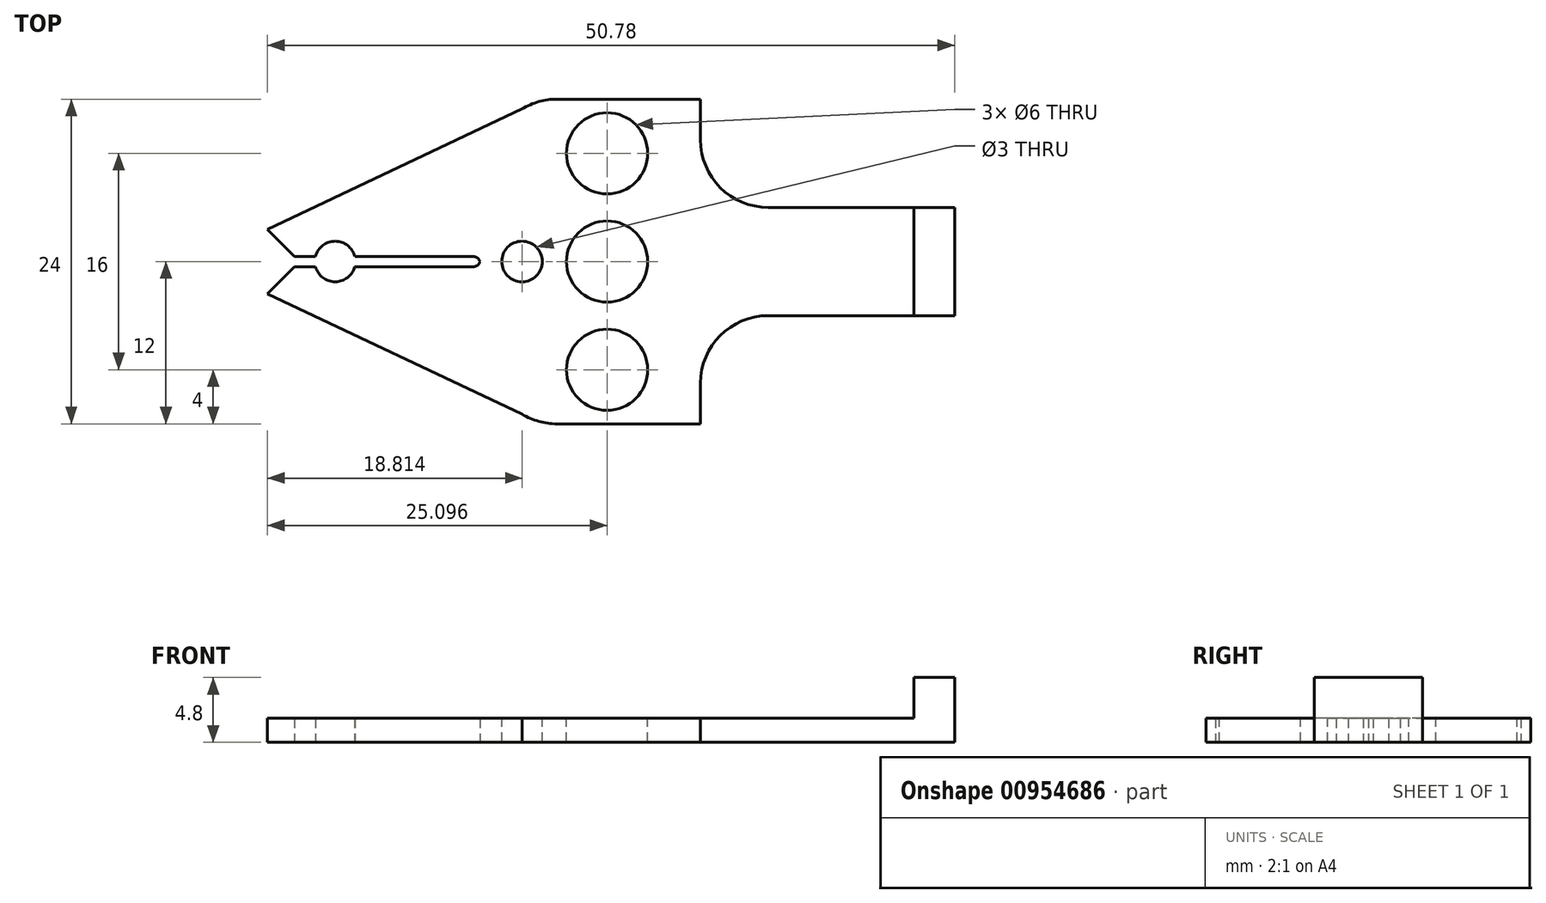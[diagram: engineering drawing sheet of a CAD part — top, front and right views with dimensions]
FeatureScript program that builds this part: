
annotation { "Feature Type Name" : "Feature", "Feature Type Description" : "" }
export const myFeature = defineFeature(function(context is Context, id is Id, definition is map)
    precondition{}
    {
        {
            var Q0;
            Q0=qCreatedBy(makeId("Top.planeOp"),FACE);
            var sketch = newSketch(context, id + "F0", { "sketchPlane" : qUnion([Q0])});
            skLineSegment(sketch, "E0.top", {"start": v(1.39, -12) * mm, "end": v(12, -12) * mm});
            skLineSegment(sketch, "E0.right", {"start": v(12, 12) * mm, "end": v(12, -12) * mm});
            skPoint(sketch, "E0.middle", {"position": v(0, 0) * mm});
            skArc(sketch, "E1", {"start": v(-16.45, -0.39) * mm, "mid": v(-15, -1.5) * mm, "end": v(-13.55, -0.39) * mm});
            skLineSegment(sketch, "E2", {"start": v(-18, 0.37) * mm, "end": v(-16.45, 0.37) * mm});
            skLineSegment(sketch, "E3", {"start": v(-18, -0.39) * mm, "end": v(-16.45, -0.39) * mm});
            skLineSegment(sketch, "E4", {"start": v(-4.3, 0.37) * mm, "end": v(-4.3, -0.39) * mm});
            skPoint(sketch, "E5.orphan", {"position": v(-12, 12) * mm});
            skPoint(sketch, "E6.orphan", {"position": v(-12, -12) * mm});
            skLineSegment(sketch, "E7", {"start": v(1.4, 12) * mm, "end": v(12, 12) * mm});
            skPoint(sketch, "E8.visualSharp", {"position": v(0, 12) * mm});
            skArc(sketch, "E8.filletArc", {"start": v(1.4, 12) * mm, "mid": v(0.05, 11.82) * mm, "end": v(-1.2, 11.28) * mm});
            skPoint(sketch, "E9.visualSharp", {"position": v(0, -12) * mm});
            skArc(sketch, "E9.filletArc", {"start": v(-1.19, -11.28) * mm, "mid": v(0.05, -11.82) * mm, "end": v(1.39, -12) * mm});
            skPoint(sketch, "E10.visualSharp", {"position": v(-19.3, -0.39) * mm});
            skPoint(sketch, "E11.visualSharp", {"position": v(-19.3, 0.37) * mm});
            skLineSegment(sketch, "E12.trimOffspring", {"start": v(-13.55, 0.37) * mm, "end": v(-4.3, 0.37) * mm});
            skLineSegment(sketch, "E13.trimOffspring", {"start": v(-13.55, -0.39) * mm, "end": v(-4.3, -0.39) * mm});
            skArc(sketch, "E14.trimOffspring", {"start": v(-13.55, 0.37) * mm, "mid": v(-15, 1.5) * mm, "end": v(-16.45, 0.37) * mm});
            skLineSegment(sketch, "E15.bottom", {"start": v(10.78, -4) * mm, "end": v(30.78, -4) * mm});
            skLineSegment(sketch, "E15.top", {"start": v(10.78, 4) * mm, "end": v(30.78, 4) * mm});
            skLineSegment(sketch, "E15.left", {"start": v(10.78, -4) * mm, "end": v(10.78, 4) * mm});
            skLineSegment(sketch, "E15.right", {"start": v(30.78, -4) * mm, "end": v(30.78, 4) * mm});
            skLineSegment(sketch, "E16", {"start": v(-18, 0.37) * mm, "end": v(-20, 2.37) * mm});
            skLineSegment(sketch, "E17", {"start": v(-18, -0.39) * mm, "end": v(-20, -2.39) * mm});
            skLineSegment(sketch, "E18", {"start": v(-20, -2.39) * mm, "end": v(-1.19, -11.28) * mm});
            skLineSegment(sketch, "E19", {"start": v(-20, 2.37) * mm, "end": v(-1.2, 11.28) * mm});
            skSolve(sketch);
        }
        {
            var Q0;
            {var subQ1=sQuery(id+"F0.wireOp",EDGE,"E0.top");Q0=makeQuery(id+"F0.imprint","IMPRINT",FACE,{"disambiguationData":[TD([[makeQuery(id+"F0.imprint","IMPRINT",EDGE,{"derivedFrom":subQ1}),1.0]])]});}
            var Q1;
            {var subQ5=sQuery(id+"F0.wireOp",EDGE,"E15.right");Q1=makeQuery(id+"F0.imprint","IMPRINT",FACE,{"disambiguationData":[TD([[makeQuery(id+"F0.imprint","IMPRINT",EDGE,{"derivedFrom":subQ5}),1.0]])]});}
            var Q2;
            {var subQ5=sQuery(id+"F0.wireOp",EDGE,"E15.left");Q2=makeQuery(id+"F0.imprint","IMPRINT",FACE,{"disambiguationData":[TD([[makeQuery(id+"F0.imprint","IMPRINT",EDGE,{"derivedFrom":subQ5}),-1.0]])]});}
            extrude(context, id + "F1", {"entities" : qUnion([Q0, Q1, Q2]), "depth" : 1.8 * mm, "offsetDistance" : 25 * mm});
        }
        {
            var Q0;
            Q0=makeQuery(id+"F1.opExtrude","CAP_FACE",FACE,{"disambiguationData":[OSD([sQuery(id+"F0.wireOp",EDGE,"E0.top"),sQuery(id+"F0.wireOp",EDGE,"E0.right"),sQuery(id+"F0.wireOp",EDGE,"E1"),sQuery(id+"F0.wireOp",EDGE,"E2"),sQuery(id+"F0.wireOp",EDGE,"E3"),sQuery(id+"F0.wireOp",EDGE,"Bz1gHbkU-Zwme-7SFB-9NIF-dOb9s8jUpKD4"),sQuery(id+"F0.wireOp",EDGE,"sMRzRCap-j28Y-DiFi-jWmF-1OPPZPiDz5Cm"),sQuery(id+"F0.wireOp",EDGE,"E4"),sQuery(id+"F0.wireOp",EDGE,"E7"),sQuery(id+"F0.wireOp",EDGE,"E8.filletArc"),sQuery(id+"F0.wireOp",EDGE,"E9.filletArc"),sQuery(id+"F0.wireOp",EDGE,"E10.filletArc"),sQuery(id+"F0.wireOp",EDGE,"E11.filletArc"),sQuery(id+"F0.wireOp",EDGE,"E12.trimOffspring"),sQuery(id+"F0.wireOp",EDGE,"E13.trimOffspring"),sQuery(id+"F0.wireOp",EDGE,"E14.trimOffspring"),sQuery(id+"F0.wireOp",EDGE,"E15.bottom"),sQuery(id+"F0.wireOp",EDGE,"E15.top"),sQuery(id+"F0.wireOp",EDGE,"E15.right")])],"isStart":false});
            var sketch = newSketch(context, id + "F2", { "sketchPlane" : qUnion([Q0])});
            skCircle(sketch, "E20", {"center": v(5.1, 0) * mm, "radius": 3 * mm});
            skCircle(sketch, "E21", {"center": v(5.1, 8) * mm, "radius": 3 * mm});
            skCircle(sketch, "E22", {"center": v(5.1, -8) * mm, "radius": 3 * mm});
            skCircle(sketch, "E23", {"center": v(-1.19, 0) * mm, "radius": 1.5 * mm});
            skSolve(sketch);
        }
        {
            var Q0;
            Q0=makeQuery(id+"F2.imprint","IMPRINT",FACE,{"disambiguationData":[TD([[makeQuery(id+"F2.imprint","IMPRINT",EDGE,{"derivedFrom":sQuery(id+"F2.wireOp",EDGE,"E21")}),1.0]])]});
            var Q1;
            Q1=makeQuery(id+"F2.imprint","IMPRINT",FACE,{"disambiguationData":[TD([[makeQuery(id+"F2.imprint","IMPRINT",EDGE,{"derivedFrom":sQuery(id+"F2.wireOp",EDGE,"E20")}),1.0]])]});
            var Q2;
            Q2=makeQuery(id+"F2.imprint","IMPRINT",FACE,{"disambiguationData":[TD([[makeQuery(id+"F2.imprint","IMPRINT",EDGE,{"derivedFrom":sQuery(id+"F2.wireOp",EDGE,"E22")}),1.0]])]});
            var Q3;
            Q3=makeQuery(id+"F2.imprint","IMPRINT",FACE,{"disambiguationData":[TD([[makeQuery(id+"F2.imprint","IMPRINT",EDGE,{"derivedFrom":sQuery(id+"F2.wireOp",EDGE,"E23")}),1.0]])]});
            extrude(context, id + "F3", {"entities" : qUnion([Q0, Q1, Q2, Q3]), "operationType" : NewBodyOperationType.REMOVE, "endBound" : BoundingType.THROUGH_ALL, "oppositeDirection" : true, "depth" : 25 * mm, "offsetDistance" : 25 * mm});
        }
        {
            var Q0;
            Q0=makeQuery(id+"F1.opExtrude","CAP_FACE",FACE,{"disambiguationData":[OSD([sQuery(id+"F0.wireOp",EDGE,"E0.top"),sQuery(id+"F0.wireOp",EDGE,"E0.right"),sQuery(id+"F0.wireOp",EDGE,"E1"),sQuery(id+"F0.wireOp",EDGE,"E2"),sQuery(id+"F0.wireOp",EDGE,"E3"),sQuery(id+"F0.wireOp",EDGE,"Bz1gHbkU-Zwme-7SFB-9NIF-dOb9s8jUpKD4"),sQuery(id+"F0.wireOp",EDGE,"sMRzRCap-j28Y-DiFi-jWmF-1OPPZPiDz5Cm"),sQuery(id+"F0.wireOp",EDGE,"E4"),sQuery(id+"F0.wireOp",EDGE,"E7"),sQuery(id+"F0.wireOp",EDGE,"E8.filletArc"),sQuery(id+"F0.wireOp",EDGE,"E9.filletArc"),sQuery(id+"F0.wireOp",EDGE,"E10.filletArc"),sQuery(id+"F0.wireOp",EDGE,"E11.filletArc"),sQuery(id+"F0.wireOp",EDGE,"E12.trimOffspring"),sQuery(id+"F0.wireOp",EDGE,"E13.trimOffspring"),sQuery(id+"F0.wireOp",EDGE,"E14.trimOffspring"),sQuery(id+"F0.wireOp",EDGE,"E15.bottom"),sQuery(id+"F0.wireOp",EDGE,"E15.top"),sQuery(id+"F0.wireOp",EDGE,"E15.right")])],"isStart":false});
            var sketch = newSketch(context, id + "F4", { "sketchPlane" : qUnion([Q0])});
            skLineSegment(sketch, "E24.bottom", {"start": v(30.78, 4) * mm, "end": v(27.78, 4) * mm});
            skLineSegment(sketch, "E24.top", {"start": v(30.78, -4) * mm, "end": v(27.78, -4) * mm});
            skLineSegment(sketch, "E24.left", {"start": v(30.78, 4) * mm, "end": v(30.78, -4) * mm});
            skLineSegment(sketch, "E24.right", {"start": v(27.78, 4) * mm, "end": v(27.78, -4) * mm});
            skSolve(sketch);
        }
        {
            var Q0;
            Q0 = qSketchRegion(id + "F4", true);
            var Q1;
            Q1=makeQuery(id+"F4.imprint","IMPRINT",FACE,{"disambiguationData":[TD([[makeQuery(id+"F4.imprint","IMPRINT",EDGE,{"derivedFrom":sQuery(id+"F4.wireOp",EDGE,"E24.bottom")}),-1.0]])]});
            extrude(context, id + "F5", {"entities" : qUnion([Q0, Q1]), "operationType" : NewBodyOperationType.ADD, "depth" : 3 * mm, "offsetDistance" : 25 * mm});
        }
        {
            var Q0;
            Q0=makeQuery(id+"F1.opExtrude","SWEPT_EDGE",EDGE,{"disambiguationData":[OSD([sQuery(id+"F0.wireOp",EDGE,"E0.right"),sQuery(id+"F0.wireOp",EDGE,"E15.top")])]});
            var Q1;
            Q1=makeQuery(id+"F1.opExtrude","SWEPT_EDGE",EDGE,{"disambiguationData":[OSD([sQuery(id+"F0.wireOp",EDGE,"E0.right"),sQuery(id+"F0.wireOp",EDGE,"E15.bottom")])]});
            fillet(context, id + "F6", {"entities" : qUnion([Q0, Q1]), "radius" : 5 * mm, "tangentPropagation" : true, "allowEdgeOverflow" : false});
        }
        {
            var Q0;
            Q0=makeQuery(id+"F1.opExtrude","SWEPT_EDGE",EDGE,{"disambiguationData":[OSD([sQuery(id+"F0.wireOp",EDGE,"E4"),sQuery(id+"F0.wireOp",EDGE,"E13.trimOffspring")])]});
            var Q1;
            Q1=makeQuery(id+"F1.opExtrude","SWEPT_EDGE",EDGE,{"disambiguationData":[OSD([sQuery(id+"F0.wireOp",EDGE,"E4"),sQuery(id+"F0.wireOp",EDGE,"E12.trimOffspring")])]});
            fillet(context, id + "F7", {"entities" : qUnion([Q0, Q1]), "radius" : .5 * mm, "tangentPropagation" : true, "allowEdgeOverflow" : false});
        }
    });
